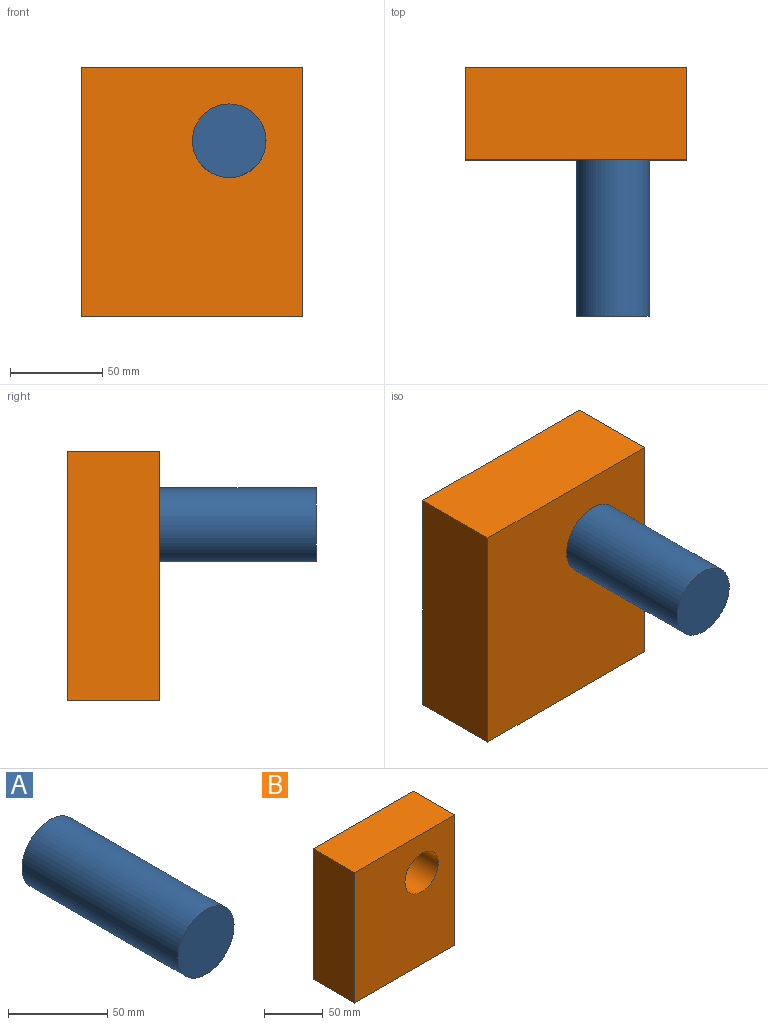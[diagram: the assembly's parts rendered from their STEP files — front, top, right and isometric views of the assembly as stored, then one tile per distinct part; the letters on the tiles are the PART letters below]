
ASSEMBLY  parts=2 mates=1
PART A: 3 faces, bbox 40x111.2x40 mm
  f0: cylinder r=20mm len=111.2mm, axis (0,1,0), area 13973.8mm2, adj f1,f2
  f1: plane 40x40mm, normal (0,-1,0), area 1256.6mm2, adj f0
  f2: plane 40x40mm, normal (0,1,0), area 1256.6mm2, adj f0
PART B: 7 faces, bbox 120.5x50x135.7 mm
  f0: plane 120.46x50mm, normal (0,0,-1), area 6022.8mm2, adj f1,f3,f4,f5
  f1: plane 135.7x50mm, normal (1,0,0), area 6784.8mm2, adj f0,f2,f4,f5
  f2: plane 120.46x50mm, normal (0,0,1), area 6022.8mm2, adj f1,f3,f4,f5
  f3: plane 135.7x50mm, normal (-1,0,0), area 6784.8mm2, adj f0,f2,f4,f5
  f4: plane 135.7x120.46mm, normal (0,-1,0), area 15088.6mm2, adj f0,f1,f2,f3,f6
  f5: plane 135.7x120.46mm, normal (0,1,0), area 15088.6mm2, adj f0,f1,f2,f3,f6
  f6: cylinder r=20mm len=50mm, axis (0,1,0), area 6283.2mm2, adj f4,f5
PLACE A rot(axis=(0,-1,0),30.6deg) t=(-87.45,6.49,121.75)mm
PLACE B t=(-47.45,30.31,26.05)mm fixed
MATE cylindrical A.f0 <-> B.f6  axis (0,1,0) through (-87.45,-49.11,121.75)mm
